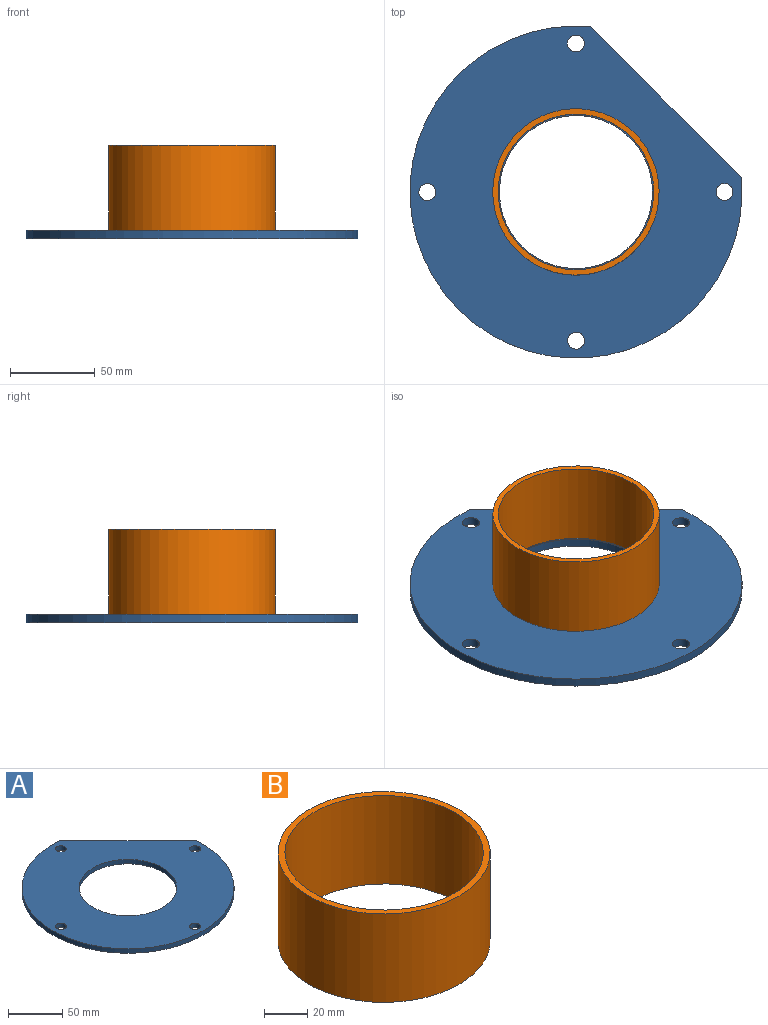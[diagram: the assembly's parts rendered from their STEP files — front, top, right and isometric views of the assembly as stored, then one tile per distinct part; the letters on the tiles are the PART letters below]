
ASSEMBLY  parts=2 mates=1
PART A: 9 faces, bbox 195.6x195.6x5 mm
  f0: cylinder r=5mm len=10mm, axis (0,0,-1), area 157.1mm2, adj f6,f7
  f1: cylinder r=5mm len=10mm, axis (0,0,-1), area 157.1mm2, adj f6,f7
  f2: cylinder r=5mm len=10mm, axis (0,0,-1), area 157.1mm2, adj f6,f7
  f3: cylinder r=5mm len=10mm, axis (0,0,-1), area 157.1mm2, adj f6,f7
  f4: cylinder r=45.09mm len=90.17mm, axis (0,0,-1), area 1416.4mm2, adj f6,f7
  f5: cylinder r=97.79mm len=195.58mm, axis (0,0,-1), area 2390.8mm2, adj f6,f7,f8
  f6: plane 195.58x195.58mm, normal (0,0,1), area 21386.5mm2, adj f0,f1,f2,f3,f4,f5,f8
  f7: plane 195.58x195.58mm, normal (0,0,-1), area 21386.5mm2, adj f0,f1,f2,f3,f4,f5,f8
  f8: plane 88.75x88.75mm, normal (0.71,0.71,0), area 627.5mm2, adj f5,f6,f7
PART B: 4 faces, bbox 98x98x50 mm
  f0: cylinder r=45.82mm len=91.65mm, axis (0,0,-1), area 14396.3mm2, adj f2,f3
  f1: cylinder r=49mm len=98mm, axis (0,0,-1), area 15393.8mm2, adj f2,f3
  f2: plane 98x98mm, normal (0,0,1), area 945.8mm2, adj f0,f1
  f3: plane 98x98mm, normal (0,0,-1), area 945.8mm2, adj f0,f1
PLACE A at identity fixed
PLACE B rot(axis=(0.45,-0.89,0),180deg) t=(0,0,30)mm
MATE revolute B.f0 <-> A.f4  axis (0,0,-1) through (0,0,5)mm
